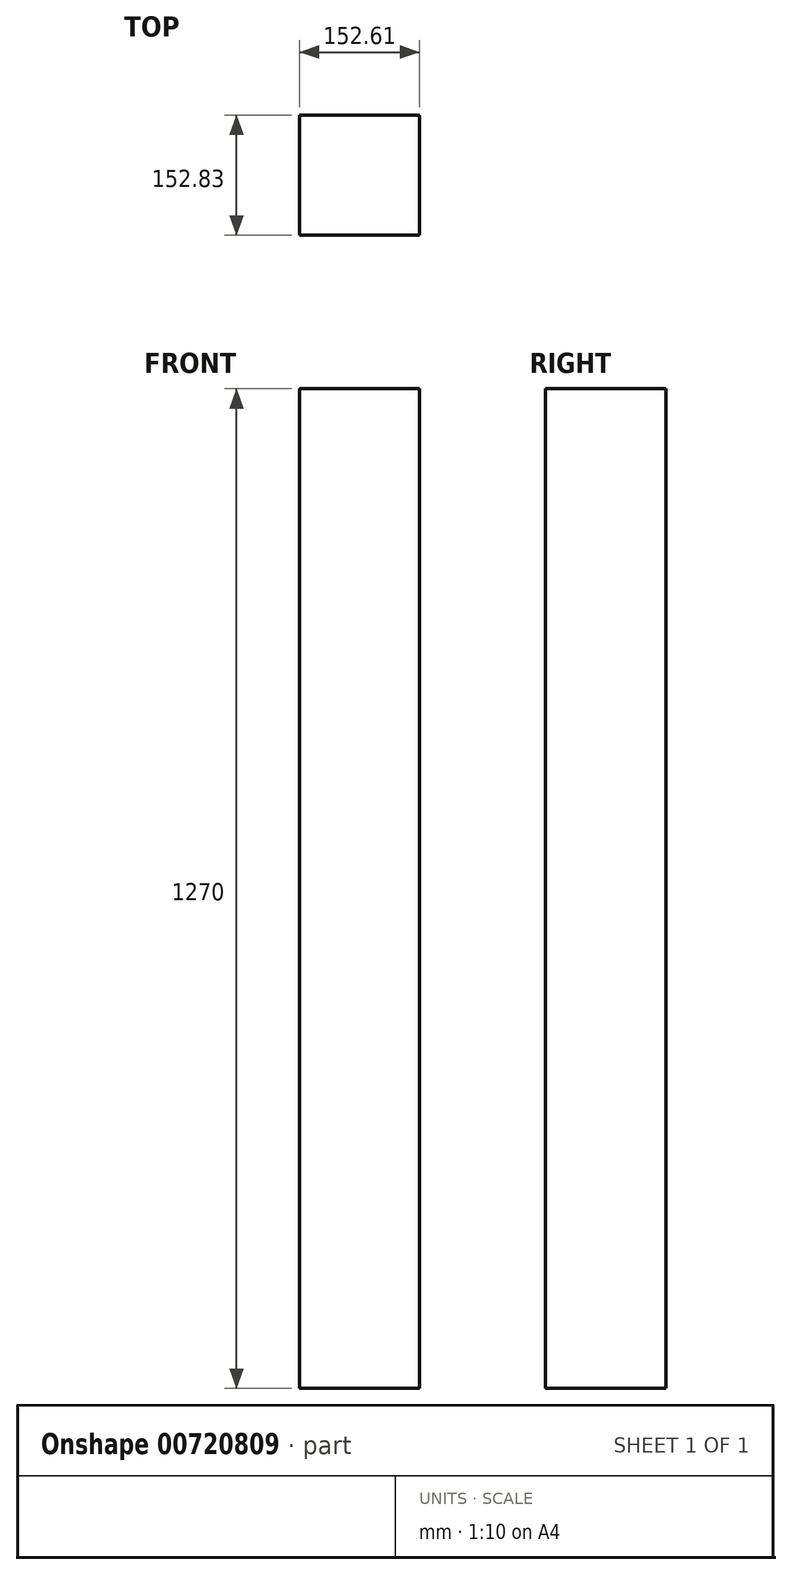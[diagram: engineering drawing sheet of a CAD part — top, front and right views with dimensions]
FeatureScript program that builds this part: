
annotation { "Feature Type Name" : "Feature", "Feature Type Description" : "" }
export const myFeature = defineFeature(function(context is Context, id is Id, definition is map)
    precondition{}
    {
        {
            var Q0;
            Q0=qCreatedBy(makeId("Top.planeOp"),FACE);
            var sketch = newSketch(context, id + "F0", { "sketchPlane" : qUnion([Q0])});
            skLineSegment(sketch, "E0.bottom", {"start": v(-75.88, 76.3) * mm, "end": v(76.73, 76.3) * mm});
            skLineSegment(sketch, "E0.top", {"start": v(-75.88, -76.52) * mm, "end": v(76.73, -76.52) * mm});
            skLineSegment(sketch, "E0.left", {"start": v(-75.88, 76.3) * mm, "end": v(-75.88, -76.52) * mm});
            skLineSegment(sketch, "E0.right", {"start": v(76.73, 76.3) * mm, "end": v(76.73, -76.52) * mm});
            skSolve(sketch);
        }
        {
            var Q0;
            Q0 = qSketchRegion(id + "F0", true);
            var Q1;
            Q1=makeQuery(id+"F0.imprint","IMPRINT",FACE,{"disambiguationData":[TD([[makeQuery(id+"F0.imprint","IMPRINT",EDGE,{"derivedFrom":sQuery(id+"F0.wireOp",EDGE,"E0.bottom")}),-1.0]])]});
            extrude(context, id + "F1", {"entities" : qUnion([Q0, Q1]), "depth" : 1270 * mm, "offsetDistance" : 25.4 * mm});
        }
    });
